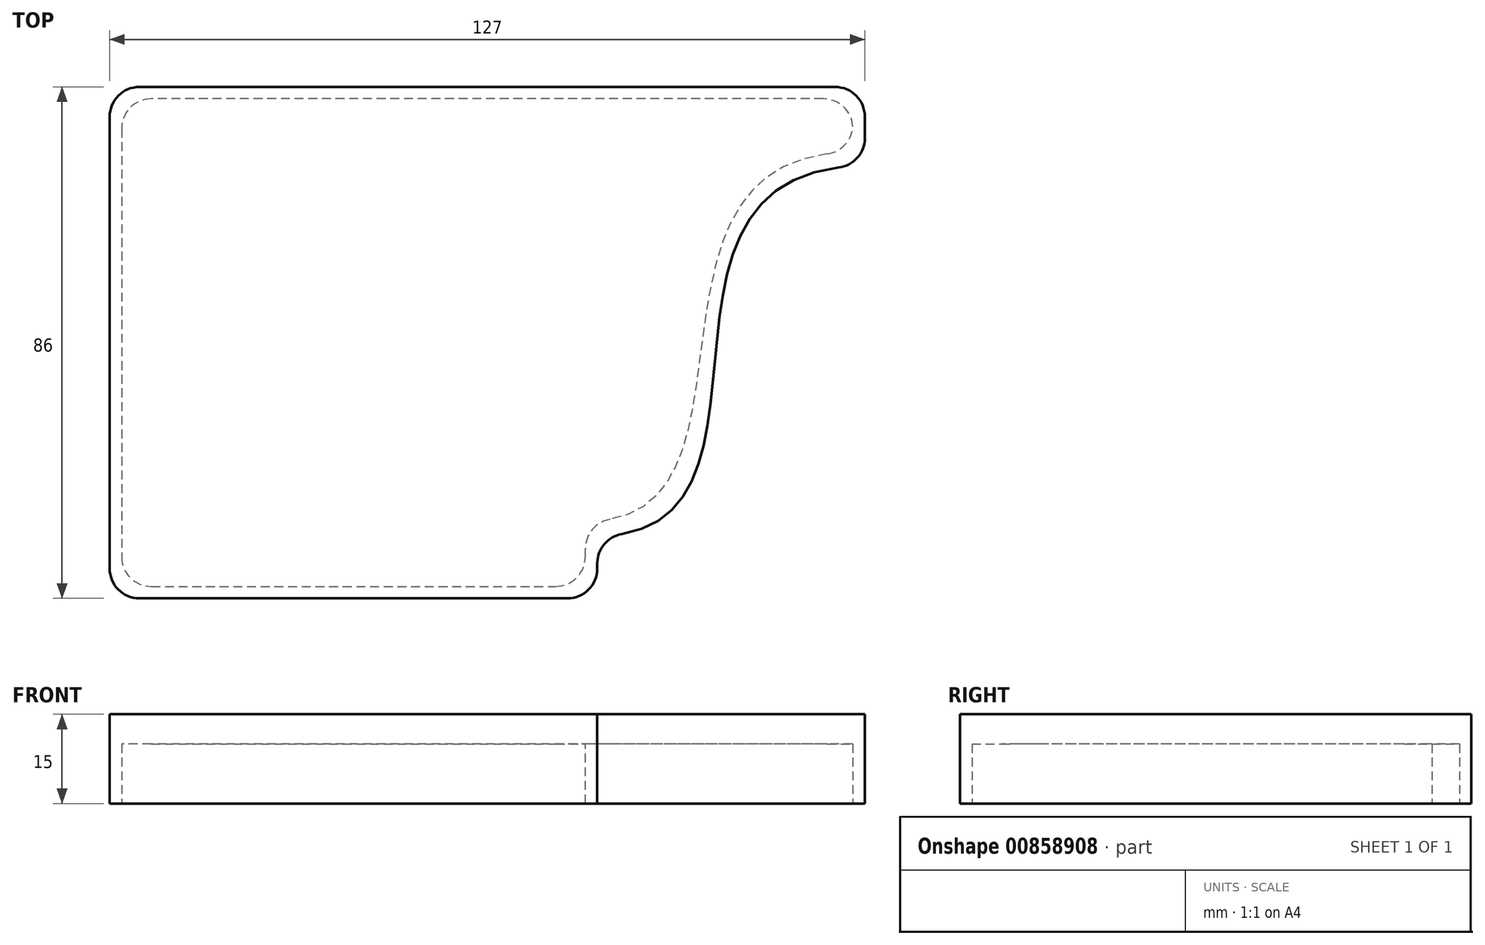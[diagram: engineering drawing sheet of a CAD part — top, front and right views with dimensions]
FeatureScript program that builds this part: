
annotation { "Feature Type Name" : "Feature", "Feature Type Description" : "" }
export const myFeature = defineFeature(function(context is Context, id is Id, definition is map)
    precondition{}
    {
        {
            var Q0;
            Q0=qCreatedBy(makeId("Top.planeOp"),FACE);
            var sketch = newSketch(context, id + "F0", { "sketchPlane" : qUnion([Q0])});
            skLineSegment(sketch, "E0", {"start": v(47.48, 30.74) * mm, "end": v(-75.52, 30.74) * mm});
            skLineSegment(sketch, "E1", {"start": v(-75.52, 30.74) * mm, "end": v(-75.52, -51.26) * mm});
            skLineSegment(sketch, "E2", {"start": v(-75.52, -51.26) * mm, "end": v(2.48, -51.26) * mm});
            skLineSegment(sketch, "E3", {"start": v(2.48, -51.26) * mm, "end": v(2.48, -40.26) * mm});
            skLineSegment(sketch, "E4", {"start": v(47.48, 30.74) * mm, "end": v(47.48, 21.74) * mm});
            skLineSegment(sketch, "E5.0", {"start": v(49.48, 32.74) * mm, "end": v(49.48, 19.46) * mm});
            skLineSegment(sketch, "E5.1", {"start": v(-77.52, 32.74) * mm, "end": v(-77.52, -53.26) * mm});
            skLineSegment(sketch, "E5.2", {"start": v(-77.52, -53.26) * mm, "end": v(4.48, -53.26) * mm});
            skLineSegment(sketch, "E5.3", {"start": v(49.48, 32.74) * mm, "end": v(-77.52, 32.74) * mm});
            skLineSegment(sketch, "E5.4", {"start": v(4.48, -53.26) * mm, "end": v(4.48, -42.77) * mm});
            skFitSpline(sketch, "E6", {"points": [v(49.48, 19.46) * mm, v(4.48, -42.77) * mm], "startDerivative": vector(-127.33, -0.8) * mm, "endDerivative": vector(-106.79, 0) * mm});
            skFitSpline(sketch, "E7", {"points": [v(47.48, 21.74) * mm, v(2.48, -40.26) * mm], "startDerivative": vector(-121.33, 0) * mm, "endDerivative": vector(-98.96, 2.15) * mm});
            skSolve(sketch);
        }
        {
            var Q0;
            Q0=makeQuery(id+"F0.imprint","IMPRINT",FACE,{"disambiguationData":[TD([[makeQuery(id+"F0.imprint","IMPRINT",EDGE,{"derivedFrom":sQuery(id+"F0.wireOp",EDGE,"E0")}),1.0]])]});
            var Q1;
            Q1=makeQuery(id+"F0.imprint","IMPRINT",FACE,{"disambiguationData":[TD([[makeQuery(id+"F0.imprint","IMPRINT",EDGE,{"derivedFrom":sQuery(id+"F0.wireOp",EDGE,"E0")}),-1.0]])]});
            extrude(context, id + "F1", {"entities" : qUnion([Q0, Q1]), "depth" : 15 * mm, "offsetDistance" : 25 * mm});
        }
        {
            var Q0;
            Q0=makeQuery(id+"F0.imprint","IMPRINT",FACE,{"disambiguationData":[TD([[makeQuery(id+"F0.imprint","IMPRINT",EDGE,{"derivedFrom":sQuery(id+"F0.wireOp",EDGE,"E0")}),1.0]])]});
            var Q1;
            Q1=sQuery(id+"F0.wireOp",EDGE,"E7");
            var Q2;
            Q2=sQuery(id+"F0.wireOp",EDGE,"E4");
            var Q3;
            Q3=sQuery(id+"F0.wireOp",EDGE,"E0");
            var Q4;
            Q4=sQuery(id+"F0.wireOp",EDGE,"E1");
            var Q5;
            Q5=sQuery(id+"F0.wireOp",EDGE,"E2");
            var Q6;
            Q6=sQuery(id+"F0.wireOp",EDGE,"E3");
            extrude(context, id + "F2", {"entities" : qUnion([Q0]), "operationType" : NewBodyOperationType.REMOVE, "surfaceEntities" : qUnion([Q1, Q2, Q3, Q4, Q5, Q6]), "depth" : 10 * mm, "offsetDistance" : 25 * mm});
        }
        {
            var Q0;
            Q0=makeQuery(id+"F2.boolean.opBoolean","COPY",EDGE,{"derivedFrom":makeQuery(id+"F2.opExtrude","SWEPT_EDGE",EDGE,{"disambiguationData":[OSD([sQuery(id+"F0.wireOp",EDGE,"E2"),sQuery(id+"F0.wireOp",EDGE,"E3")])]})});
            var Q1;
            Q1=makeQuery(id+"F2.boolean.opBoolean","COPY",EDGE,{"derivedFrom":makeQuery(id+"F2.opExtrude","SWEPT_EDGE",EDGE,{"disambiguationData":[OSD([sQuery(id+"F0.wireOp",EDGE,"E3"),sQuery(id+"F0.wireOp",EDGE,"E7")])]})});
            var Q2;
            Q2=makeQuery(id+"F2.boolean.opBoolean","COPY",EDGE,{"derivedFrom":makeQuery(id+"F2.opExtrude","SWEPT_EDGE",EDGE,{"disambiguationData":[OSD([sQuery(id+"F0.wireOp",EDGE,"E1"),sQuery(id+"F0.wireOp",EDGE,"E2")])]})});
            var Q3;
            Q3=makeQuery(id+"F2.boolean.opBoolean","COPY",EDGE,{"derivedFrom":makeQuery(id+"F2.opExtrude","SWEPT_EDGE",EDGE,{"disambiguationData":[OSD([sQuery(id+"F0.wireOp",EDGE,"E0"),sQuery(id+"F0.wireOp",EDGE,"E4")])]})});
            var Q4;
            Q4=makeQuery(id+"F2.boolean.opBoolean","COPY",EDGE,{"derivedFrom":makeQuery(id+"F2.opExtrude","SWEPT_EDGE",EDGE,{"disambiguationData":[OSD([sQuery(id+"F0.wireOp",EDGE,"E4"),sQuery(id+"F0.wireOp",EDGE,"E7")])]})});
            var Q5;
            Q5=makeQuery(id+"F2.boolean.opBoolean","COPY",EDGE,{"derivedFrom":makeQuery(id+"F2.opExtrude","SWEPT_EDGE",EDGE,{"disambiguationData":[OSD([sQuery(id+"F0.wireOp",EDGE,"E0"),sQuery(id+"F0.wireOp",EDGE,"E1")])]})});
            var Q6;
            Q6=makeQuery(id+"F1.opExtrude","SWEPT_EDGE",EDGE,{"disambiguationData":[OSD([sQuery(id+"F0.wireOp",EDGE,"E5.1"),sQuery(id+"F0.wireOp",EDGE,"E5.3")])]});
            var Q7;
            Q7=makeQuery(id+"F1.opExtrude","SWEPT_EDGE",EDGE,{"disambiguationData":[OSD([sQuery(id+"F0.wireOp",EDGE,"E5.1"),sQuery(id+"F0.wireOp",EDGE,"E5.2")])]});
            var Q8;
            Q8=makeQuery(id+"F1.opExtrude","SWEPT_EDGE",EDGE,{"disambiguationData":[OSD([sQuery(id+"F0.wireOp",EDGE,"E5.2"),sQuery(id+"F0.wireOp",EDGE,"E5.4")])]});
            var Q9;
            Q9=makeQuery(id+"F1.opExtrude","SWEPT_EDGE",EDGE,{"disambiguationData":[OSD([sQuery(id+"F0.wireOp",EDGE,"E5.4"),sQuery(id+"F0.wireOp",EDGE,"E6")])]});
            var Q10;
            Q10=makeQuery(id+"F1.opExtrude","SWEPT_EDGE",EDGE,{"disambiguationData":[OSD([sQuery(id+"F0.wireOp",EDGE,"E5.0"),sQuery(id+"F0.wireOp",EDGE,"E6")])]});
            var Q11;
            Q11=makeQuery(id+"F1.opExtrude","SWEPT_EDGE",EDGE,{"disambiguationData":[OSD([sQuery(id+"F0.wireOp",EDGE,"E5.0"),sQuery(id+"F0.wireOp",EDGE,"E5.3")])]});
            fillet(context, id + "F3", {"entities" : qUnion([Q0, Q1, Q2, Q3, Q4, Q5, Q6, Q7, Q8, Q9, Q10, Q11]), "radius" : 5 * mm, "tangentPropagation" : true, "allowEdgeOverflow" : false});
        }
    });
